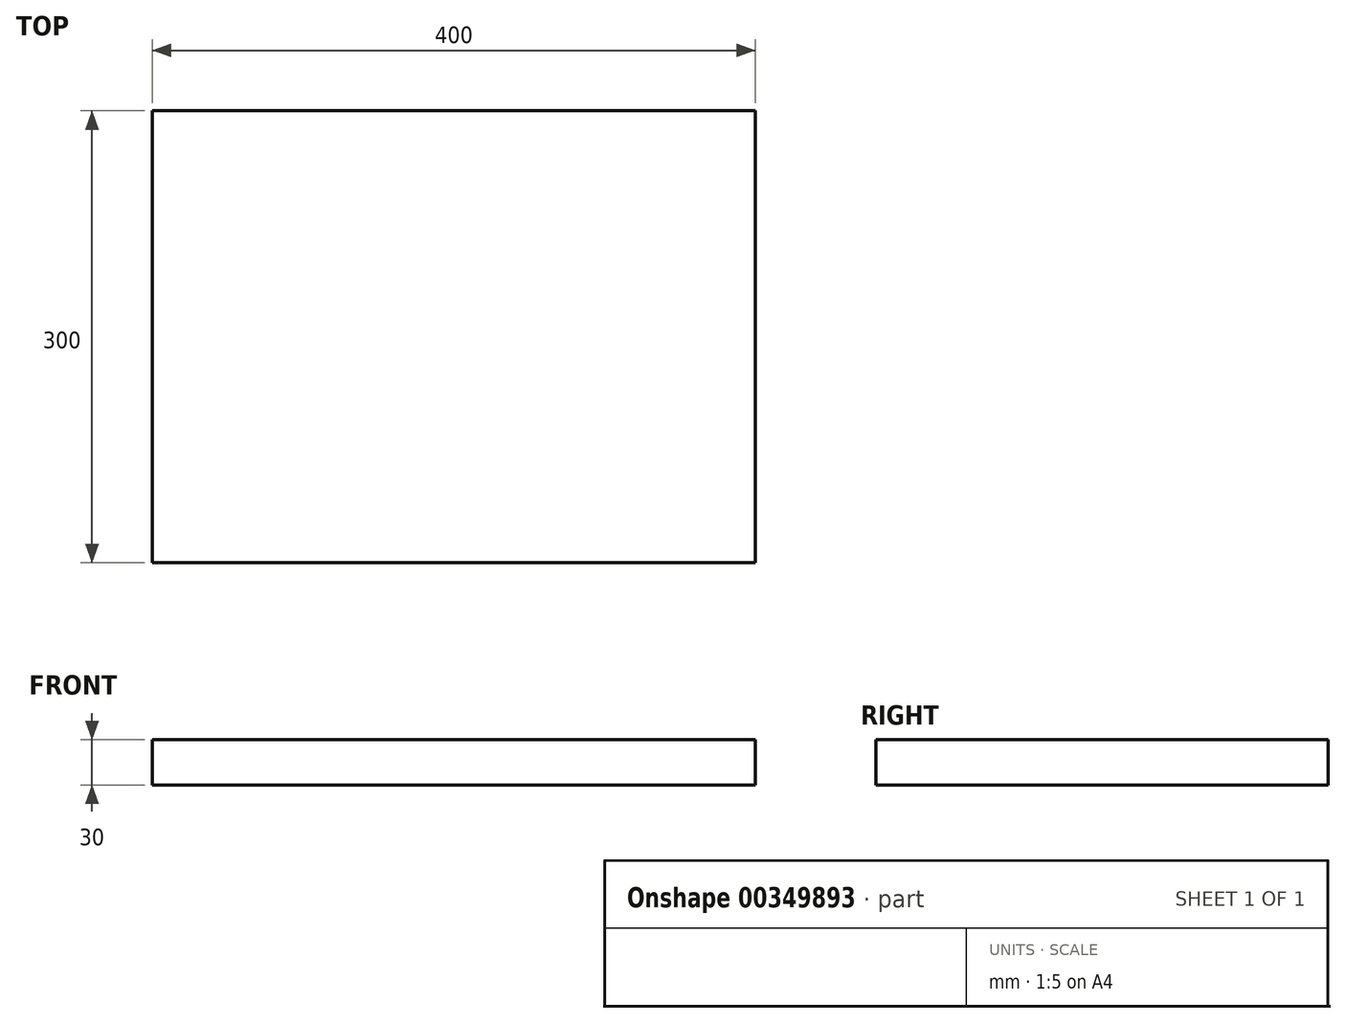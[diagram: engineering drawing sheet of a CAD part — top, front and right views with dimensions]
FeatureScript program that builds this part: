
annotation { "Feature Type Name" : "Feature", "Feature Type Description" : "" }
export const myFeature = defineFeature(function(context is Context, id is Id, definition is map)
    precondition{}
    {
        {
            var Q0;
            Q0=qCreatedBy(makeId("Top.planeOp"),FACE);
            var sketch = newSketch(context, id + "F0", { "sketchPlane" : qUnion([Q0])});
            skLineSegment(sketch, "E0.bottom", {"start": v(0, 0) * mm, "end": v(400, 0) * mm});
            skLineSegment(sketch, "E0.top", {"start": v(0, -300) * mm, "end": v(400, -300) * mm});
            skLineSegment(sketch, "E0.left", {"start": v(0, 0) * mm, "end": v(0, -300) * mm});
            skLineSegment(sketch, "E0.right", {"start": v(400, 0) * mm, "end": v(400, -300) * mm});
            skSolve(sketch);
        }
        {
            var Q0;
            Q0 = qSketchRegion(id + "F0", true);
            extrude(context, id + "F1", {"entities" : qUnion([Q0]), "depth" : 30 * mm});
        }
    });
